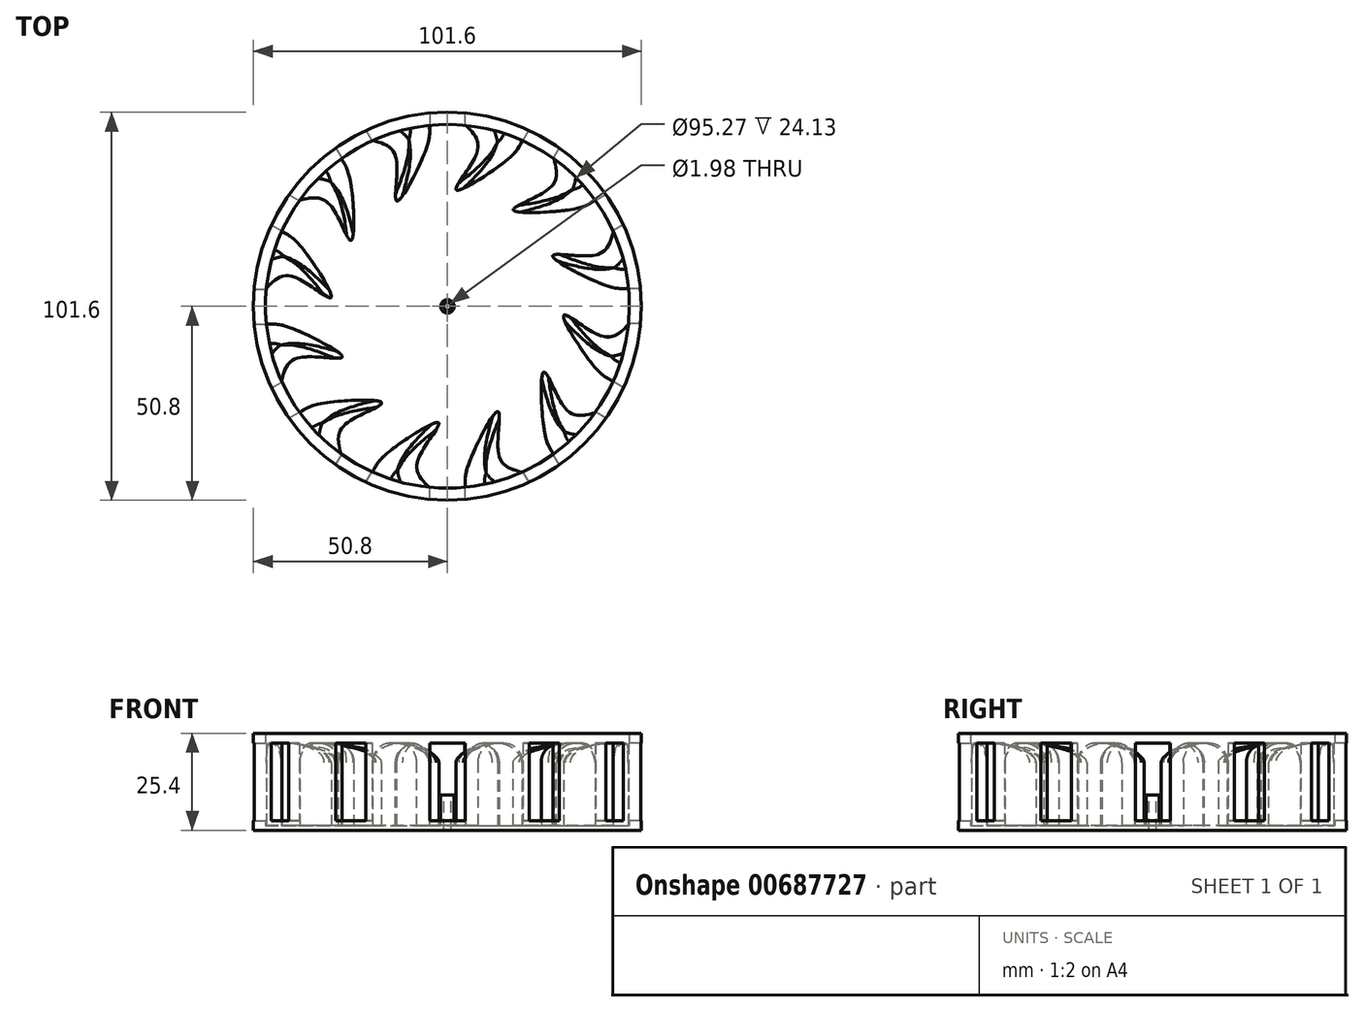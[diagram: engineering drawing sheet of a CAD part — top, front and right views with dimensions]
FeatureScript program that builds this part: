
annotation { "Feature Type Name" : "Feature", "Feature Type Description" : "" }
export const myFeature = defineFeature(function(context is Context, id is Id, definition is map)
    precondition{}
    {
        {
            var Q0;
            Q0=qCreatedBy(makeId("Top.planeOp"),FACE);
            var sketch = newSketch(context, id + "F0", { "sketchPlane" : qUnion([Q0])});
            skCircle(sketch, "E0", {"center": v(0, 0) * mm, "radius": 50.8 * mm});
            skSolve(sketch);
        }
        {
            var Q0;
            Q0=makeQuery(id+"F0.imprint","IMPRINT",FACE,{"disambiguationData":[TD([[makeQuery(id+"F0.imprint","IMPRINT",EDGE,{"derivedFrom":sQuery(id+"F0.wireOp",EDGE,"E0")}),1.0]])]});
            extrude(context, id + "F1", {"entities" : qUnion([Q0]), "depth" : 1.27 * mm, "offsetDistance" : 25.4 * mm});
        }
        {
            var Q0;
            Q0=makeQuery(id+"F1.opExtrude","CAP_FACE",FACE,{"disambiguationData":[OSD([sQuery(id+"F0.wireOp",EDGE,"E0")])],"isStart":false});
            var sketch = newSketch(context, id + "F2", { "sketchPlane" : qUnion([Q0])});
            skCircle(sketch, "E1", {"center": v(0, 0) * mm, "radius": 47.64 * mm});
            skLineSegment(sketch, "E2", {"start": v(0, 47.64) * mm, "end": v(0, -47.64) * mm});
            skLineSegment(sketch, "E3", {"start": v(-47.64, 0) * mm, "end": v(47.64, 0) * mm});
            skCircle(sketch, "E4.cCircle", {"center": v(0, 0) * mm, "radius": 17.07 * mm, "construction": true});
            skLineSegment(sketch, "E4.0", {"start": v(12.5, -12.5) * mm, "end": v(4.58, -17.07) * mm});
            skLineSegment(sketch, "E4.1", {"start": v(4.58, -17.07) * mm, "end": v(-4.57, -17.07) * mm});
            skLineSegment(sketch, "E4.2", {"start": v(-4.57, -17.07) * mm, "end": v(-12.5, -12.5) * mm});
            skLineSegment(sketch, "E4.3", {"start": v(-12.5, -12.5) * mm, "end": v(-17.07, -4.58) * mm});
            skLineSegment(sketch, "E4.4", {"start": v(-17.07, -4.58) * mm, "end": v(-17.07, 4.57) * mm});
            skLineSegment(sketch, "E4.5", {"start": v(-17.07, 4.57) * mm, "end": v(-12.5, 12.5) * mm});
            skLineSegment(sketch, "E4.6", {"start": v(-12.5, 12.5) * mm, "end": v(-4.58, 17.07) * mm});
            skLineSegment(sketch, "E4.7", {"start": v(-4.58, 17.07) * mm, "end": v(4.57, 17.07) * mm});
            skLineSegment(sketch, "E4.8", {"start": v(4.57, 17.07) * mm, "end": v(12.5, 12.5) * mm});
            skLineSegment(sketch, "E4.9", {"start": v(12.5, 12.5) * mm, "end": v(17.07, 4.58) * mm});
            skLineSegment(sketch, "E4.10", {"start": v(17.07, 4.58) * mm, "end": v(17.07, -4.57) * mm});
            skLineSegment(sketch, "E4.11", {"start": v(17.07, -4.57) * mm, "end": v(12.5, -12.5) * mm});
            skPoint(sketch, "E4.0.midPoint", {"position": v(8.54, -14.78) * mm});
            skSolve(sketch);
        }
        {
            var Q0;
            Q0=makeQuery(id+"F2.imprint","IMPRINT",FACE,{"disambiguationData":[TD([[makeQuery(id+"F2.imprint","IMPRINT",EDGE,{"derivedFrom":sQuery(id+"F2.wireOp",EDGE,"E1")}),-1.0]])]});
            extrude(context, id + "F3", {"entities" : qUnion([Q0]), "operationType" : NewBodyOperationType.ADD, "depth" : 24.13 * mm, "offsetDistance" : 25.4 * mm});
        }
        {
            var Q0;
            {var subQ0=sQuery(id+"F2.wireOp",EDGE,"E4.5");Q0=makeQuery(id+"F2.imprint","IMPRINT",FACE,{"disambiguationData":[TD([[makeQuery(id+"F2.imprint","IMPRINT",EDGE,{"derivedFrom":subQ0}),-1.0]])]});}
            var Q1;
            {var subQ0=sQuery(id+"F2.wireOp",EDGE,"E4.8");Q1=makeQuery(id+"F2.imprint","IMPRINT",FACE,{"disambiguationData":[TD([[makeQuery(id+"F2.imprint","IMPRINT",EDGE,{"derivedFrom":subQ0}),-1.0]])]});}
            var Q2;
            {var subQ1=sQuery(id+"F2.wireOp",EDGE,"E4.0");Q2=makeQuery(id+"F2.imprint","IMPRINT",FACE,{"disambiguationData":[TD([[makeQuery(id+"F2.imprint","IMPRINT",EDGE,{"derivedFrom":subQ1}),-1.0]])]});}
            var Q3;
            {var subQ0=sQuery(id+"F2.wireOp",EDGE,"E4.2");Q3=makeQuery(id+"F2.imprint","IMPRINT",FACE,{"disambiguationData":[TD([[makeQuery(id+"F2.imprint","IMPRINT",EDGE,{"derivedFrom":subQ0}),-1.0]])]});}
            extrude(context, id + "F4", {"entities" : qUnion([Q0, Q1, Q2, Q3]), "operationType" : NewBodyOperationType.ADD, "depth" : 21.59 * mm, "offsetDistance" : 25.4 * mm});
        }
        {
            var Q0;
            Q0=makeQuery(id+"F4.opExtrude","SWEPT_FACE",FACE,{"disambiguationData":[OSD([sQuery(id+"F2.wireOp",EDGE,"E4.1")])]});
            var sketch = newSketch(context, id + "F5", { "sketchPlane" : qUnion([Q0])});
            skLineSegment(sketch, "E5", {"start": v(-4.57, 2.54) * mm, "end": v(4.57, 2.54) * mm});
            skSolve(sketch);
        }
        {
            var Q0;
            Q0=makeQuery(id+"F4.opExtrude","SWEPT_FACE",FACE,{"disambiguationData":[OSD([sQuery(id+"F2.wireOp",EDGE,"E4.0")])]});
            var sketch = newSketch(context, id + "F6", { "sketchPlane" : qUnion([Q0])});
            skLineSegment(sketch, "E6", {"start": v(-4.57, 2.54) * mm, "end": v(4.57, 2.54) * mm});
            skSolve(sketch);
        }
        {
            var Q0;
            Q0=makeQuery(id+"F4.opExtrude","SWEPT_FACE",FACE,{"disambiguationData":[OSD([sQuery(id+"F2.wireOp",EDGE,"E4.11")])]});
            var sketch = newSketch(context, id + "F7", { "sketchPlane" : qUnion([Q0])});
            skLineSegment(sketch, "E7", {"start": v(-4.57, 2.54) * mm, "end": v(4.57, 2.54) * mm});
            skSolve(sketch);
        }
        {
            var Q0;
            {var subQ0=sQuery(id+"F5.wireOp",EDGE,"E5");Q0=makeQuery(id+"F5.imprint","IMPRINT",FACE,{"disambiguationData":[TD([[makeQuery(id+"F5.imprint","IMPRINT",EDGE,{"derivedFrom":subQ0}),1.0]])]});}
            extrude(context, id + "F8", {"entities" : qUnion([Q0]), "operationType" : NewBodyOperationType.REMOVE, "depth" : 50.8 * mm, "offsetDistance" : 25.4 * mm});
        }
        {
            var Q0;
            {var subQ0=sQuery(id+"F6.wireOp",EDGE,"E6");Q0=makeQuery(id+"F6.imprint","IMPRINT",FACE,{"disambiguationData":[TD([[makeQuery(id+"F6.imprint","IMPRINT",EDGE,{"derivedFrom":subQ0}),1.0]])]});}
            extrude(context, id + "F9", {"entities" : qUnion([Q0]), "operationType" : NewBodyOperationType.REMOVE, "depth" : 50.8 * mm, "offsetDistance" : 25.4 * mm});
        }
        {
            var Q0;
            {var subQ0=sQuery(id+"F7.wireOp",EDGE,"E7");Q0=makeQuery(id+"F7.imprint","IMPRINT",FACE,{"disambiguationData":[TD([[makeQuery(id+"F7.imprint","IMPRINT",EDGE,{"derivedFrom":subQ0}),1.0]])]});}
            extrude(context, id + "F10", {"entities" : qUnion([Q0]), "operationType" : NewBodyOperationType.REMOVE, "depth" : 50.8 * mm, "offsetDistance" : 25.4 * mm});
        }
        {
            var Q0;
            Q0=makeQuery(id+"F4.opExtrude","SWEPT_FACE",FACE,{"disambiguationData":[OSD([sQuery(id+"F2.wireOp",EDGE,"E4.10")])]});
            var sketch = newSketch(context, id + "F11", { "sketchPlane" : qUnion([Q0])});
            skLineSegment(sketch, "E8", {"start": v(-4.57, 2.54) * mm, "end": v(4.57, 2.54) * mm});
            skSolve(sketch);
        }
        {
            var Q0;
            Q0=makeQuery(id+"F4.opExtrude","SWEPT_FACE",FACE,{"disambiguationData":[OSD([sQuery(id+"F2.wireOp",EDGE,"E4.9")])]});
            var sketch = newSketch(context, id + "F12", { "sketchPlane" : qUnion([Q0])});
            skLineSegment(sketch, "E9", {"start": v(-4.57, 2.54) * mm, "end": v(4.57, 2.54) * mm});
            skSolve(sketch);
        }
        {
            var Q0;
            {var subQ0=sQuery(id+"F11.wireOp",EDGE,"E8");Q0=makeQuery(id+"F11.imprint","IMPRINT",FACE,{"disambiguationData":[TD([[makeQuery(id+"F11.imprint","IMPRINT",EDGE,{"derivedFrom":subQ0}),1.0]])]});}
            extrude(context, id + "F13", {"entities" : qUnion([Q0]), "operationType" : NewBodyOperationType.REMOVE, "depth" : 50.8 * mm, "offsetDistance" : 25.4 * mm});
        }
        {
            var Q0;
            {var subQ0=sQuery(id+"F12.wireOp",EDGE,"E9");Q0=makeQuery(id+"F12.imprint","IMPRINT",FACE,{"disambiguationData":[TD([[makeQuery(id+"F12.imprint","IMPRINT",EDGE,{"derivedFrom":subQ0}),1.0]])]});}
            extrude(context, id + "F14", {"entities" : qUnion([Q0]), "operationType" : NewBodyOperationType.REMOVE, "depth" : 50.8 * mm, "offsetDistance" : 25.4 * mm});
        }
        {
            var Q0;
            Q0=makeQuery(id+"F4.opExtrude","SWEPT_FACE",FACE,{"disambiguationData":[OSD([sQuery(id+"F2.wireOp",EDGE,"E4.8")])]});
            var sketch = newSketch(context, id + "F15", { "sketchPlane" : qUnion([Q0])});
            skLineSegment(sketch, "E10", {"start": v(-4.57, 2.54) * mm, "end": v(4.57, 2.54) * mm});
            skSolve(sketch);
        }
        {
            var Q0;
            Q0=makeQuery(id+"F4.opExtrude","SWEPT_FACE",FACE,{"disambiguationData":[OSD([sQuery(id+"F2.wireOp",EDGE,"E4.7")])]});
            var sketch = newSketch(context, id + "F16", { "sketchPlane" : qUnion([Q0])});
            skLineSegment(sketch, "E11", {"start": v(-4.57, 2.54) * mm, "end": v(4.57, 2.54) * mm});
            skSolve(sketch);
        }
        {
            var Q0;
            Q0=makeQuery(id+"F4.opExtrude","SWEPT_FACE",FACE,{"disambiguationData":[OSD([sQuery(id+"F2.wireOp",EDGE,"E4.6")])]});
            var sketch = newSketch(context, id + "F17", { "sketchPlane" : qUnion([Q0])});
            skLineSegment(sketch, "E12", {"start": v(-4.57, 2.54) * mm, "end": v(4.57, 2.54) * mm});
            skSolve(sketch);
        }
        {
            var Q0;
            {var subQ0=sQuery(id+"F15.wireOp",EDGE,"E10");Q0=makeQuery(id+"F15.imprint","IMPRINT",FACE,{"disambiguationData":[TD([[makeQuery(id+"F15.imprint","IMPRINT",EDGE,{"derivedFrom":subQ0}),1.0]])]});}
            extrude(context, id + "F18", {"entities" : qUnion([Q0]), "operationType" : NewBodyOperationType.REMOVE, "depth" : 50.8 * mm, "offsetDistance" : 25.4 * mm});
        }
        {
            var Q0;
            {var subQ0=sQuery(id+"F16.wireOp",EDGE,"E11");Q0=makeQuery(id+"F16.imprint","IMPRINT",FACE,{"disambiguationData":[TD([[makeQuery(id+"F16.imprint","IMPRINT",EDGE,{"derivedFrom":subQ0}),1.0]])]});}
            extrude(context, id + "F19", {"entities" : qUnion([Q0]), "operationType" : NewBodyOperationType.REMOVE, "depth" : 50.8 * mm, "offsetDistance" : 25.4 * mm});
        }
        {
            var Q0;
            {var subQ0=sQuery(id+"F17.wireOp",EDGE,"E12");Q0=makeQuery(id+"F17.imprint","IMPRINT",FACE,{"disambiguationData":[TD([[makeQuery(id+"F17.imprint","IMPRINT",EDGE,{"derivedFrom":subQ0}),1.0]])]});}
            extrude(context, id + "F20", {"entities" : qUnion([Q0]), "operationType" : NewBodyOperationType.REMOVE, "depth" : 50.8 * mm, "offsetDistance" : 25.4 * mm});
        }
        {
            var Q0;
            Q0=makeQuery(id+"F4.opExtrude","SWEPT_FACE",FACE,{"disambiguationData":[OSD([sQuery(id+"F2.wireOp",EDGE,"E4.5")])]});
            var sketch = newSketch(context, id + "F21", { "sketchPlane" : qUnion([Q0])});
            skLineSegment(sketch, "E13", {"start": v(-4.57, 2.54) * mm, "end": v(4.57, 2.54) * mm});
            skSolve(sketch);
        }
        {
            var Q0;
            Q0=makeQuery(id+"F4.opExtrude","SWEPT_FACE",FACE,{"disambiguationData":[OSD([sQuery(id+"F2.wireOp",EDGE,"E4.4")])]});
            var sketch = newSketch(context, id + "F22", { "sketchPlane" : qUnion([Q0])});
            skLineSegment(sketch, "E14", {"start": v(-4.57, 2.54) * mm, "end": v(4.57, 2.54) * mm});
            skSolve(sketch);
        }
        {
            var Q0;
            Q0=makeQuery(id+"F4.opExtrude","SWEPT_FACE",FACE,{"disambiguationData":[OSD([sQuery(id+"F2.wireOp",EDGE,"E4.3")])]});
            var sketch = newSketch(context, id + "F23", { "sketchPlane" : qUnion([Q0])});
            skLineSegment(sketch, "E15", {"start": v(-4.57, 2.54) * mm, "end": v(4.57, 2.54) * mm});
            skSolve(sketch);
        }
        {
            var Q0;
            Q0=makeQuery(id+"F4.opExtrude","SWEPT_FACE",FACE,{"disambiguationData":[OSD([sQuery(id+"F2.wireOp",EDGE,"E4.2")])]});
            var sketch = newSketch(context, id + "F24", { "sketchPlane" : qUnion([Q0])});
            skLineSegment(sketch, "E16", {"start": v(-4.57, 2.54) * mm, "end": v(4.57, 2.54) * mm});
            skSolve(sketch);
        }
        {
            var Q0;
            {var subQ0=sQuery(id+"F21.wireOp",EDGE,"E13");Q0=makeQuery(id+"F21.imprint","IMPRINT",FACE,{"disambiguationData":[TD([[makeQuery(id+"F21.imprint","IMPRINT",EDGE,{"derivedFrom":subQ0}),1.0]])]});}
            extrude(context, id + "F25", {"entities" : qUnion([Q0]), "operationType" : NewBodyOperationType.REMOVE, "depth" : 50.8 * mm, "offsetDistance" : 25.4 * mm});
        }
        {
            var Q0;
            {var subQ0=sQuery(id+"F22.wireOp",EDGE,"E14");Q0=makeQuery(id+"F22.imprint","IMPRINT",FACE,{"disambiguationData":[TD([[makeQuery(id+"F22.imprint","IMPRINT",EDGE,{"derivedFrom":subQ0}),1.0]])]});}
            extrude(context, id + "F26", {"entities" : qUnion([Q0]), "operationType" : NewBodyOperationType.REMOVE, "depth" : 50.8 * mm, "offsetDistance" : 25.4 * mm});
        }
        {
            var Q0;
            {var subQ0=sQuery(id+"F23.wireOp",EDGE,"E15");Q0=makeQuery(id+"F23.imprint","IMPRINT",FACE,{"disambiguationData":[TD([[makeQuery(id+"F23.imprint","IMPRINT",EDGE,{"derivedFrom":subQ0}),1.0]])]});}
            extrude(context, id + "F27", {"entities" : qUnion([Q0]), "operationType" : NewBodyOperationType.REMOVE, "depth" : 50.8 * mm, "offsetDistance" : 25.4 * mm});
        }
        {
            var Q0;
            {var subQ0=sQuery(id+"F24.wireOp",EDGE,"E16");Q0=makeQuery(id+"F24.imprint","IMPRINT",FACE,{"disambiguationData":[TD([[makeQuery(id+"F24.imprint","IMPRINT",EDGE,{"derivedFrom":subQ0}),1.0]])]});}
            extrude(context, id + "F28", {"entities" : qUnion([Q0]), "operationType" : NewBodyOperationType.REMOVE, "depth" : 50.8 * mm, "offsetDistance" : 25.4 * mm});
        }
        {
            var Q0;
            Q0=makeQuery(id+"F4.opExtrude","CAP_FACE",FACE,{"disambiguationData":[OSD([sQuery(id+"F2.wireOp",EDGE,"E4.0"),sQuery(id+"F2.wireOp",EDGE,"E4.1"),sQuery(id+"F2.wireOp",EDGE,"E4.2"),sQuery(id+"F2.wireOp",EDGE,"E4.3"),sQuery(id+"F2.wireOp",EDGE,"E4.4"),sQuery(id+"F2.wireOp",EDGE,"E4.5"),sQuery(id+"F2.wireOp",EDGE,"E4.6"),sQuery(id+"F2.wireOp",EDGE,"E4.7"),sQuery(id+"F2.wireOp",EDGE,"E4.8"),sQuery(id+"F2.wireOp",EDGE,"E4.9"),sQuery(id+"F2.wireOp",EDGE,"E4.10"),sQuery(id+"F2.wireOp",EDGE,"E4.11")])],"isStart":false});
            extrude(context, id + "F29", {"entities" : qUnion([Q0]), "operationType" : NewBodyOperationType.REMOVE, "oppositeDirection" : true, "depth" : 21.59 * mm, "offsetDistance" : 25.4 * mm});
        }
        {
            var Q0;
            Q0=makeQuery(id+"F29.boolean.opBoolean","MERGE",FACE,{"derivedFrom":[makeQuery(id+"F1.opExtrude","CAP_FACE",FACE,{"disambiguationData":[OSD([sQuery(id+"F0.wireOp",EDGE,"E0")])],"isStart":false}),makeQuery(id+"F29.opExtrude","CAP_FACE",FACE,{"disambiguationData":[OSD([sQuery(id+"F2.wireOp",EDGE,"E4.0"),sQuery(id+"F2.wireOp",EDGE,"E4.1"),sQuery(id+"F2.wireOp",EDGE,"E4.2"),sQuery(id+"F2.wireOp",EDGE,"E4.3"),sQuery(id+"F2.wireOp",EDGE,"E4.4"),sQuery(id+"F2.wireOp",EDGE,"E4.5"),sQuery(id+"F2.wireOp",EDGE,"E4.6"),sQuery(id+"F2.wireOp",EDGE,"E4.7"),sQuery(id+"F2.wireOp",EDGE,"E4.8"),sQuery(id+"F2.wireOp",EDGE,"E4.9"),sQuery(id+"F2.wireOp",EDGE,"E4.10"),sQuery(id+"F2.wireOp",EDGE,"E4.11")])],"isStart":false})]});
            var sketch = newSketch(context, id + "F30", { "sketchPlane" : qUnion([Q0])});
            skCircle(sketch, "E17", {"center": v(0, 0) * mm, "radius": 1 * mm});
            skCircle(sketch, "E18", {"center": v(0, 0) * mm, "radius": 1.77 * mm});
            skSolve(sketch);
        }
        {
            var Q0;
            Q0=makeQuery(id+"F30.imprint","IMPRINT",FACE,{"disambiguationData":[TD([[makeQuery(id+"F30.imprint","IMPRINT",EDGE,{"derivedFrom":sQuery(id+"F30.wireOp",EDGE,"E17")}),1.0]])]});
            extrude(context, id + "F31", {"entities" : qUnion([Q0]), "operationType" : NewBodyOperationType.REMOVE, "oppositeDirection" : true, "depth" : 25.4 * mm, "offsetDistance" : 25.4 * mm});
        }
        {
            var Q0;
            Q0=makeQuery(id+"F29.boolean.opBoolean","MERGE",FACE,{"derivedFrom":[makeQuery(id+"F1.opExtrude","CAP_FACE",FACE,{"disambiguationData":[OSD([sQuery(id+"F0.wireOp",EDGE,"E0")])],"isStart":false}),makeQuery(id+"F29.opExtrude","CAP_FACE",FACE,{"disambiguationData":[OSD([sQuery(id+"F2.wireOp",EDGE,"E4.0"),sQuery(id+"F2.wireOp",EDGE,"E4.1"),sQuery(id+"F2.wireOp",EDGE,"E4.2"),sQuery(id+"F2.wireOp",EDGE,"E4.3"),sQuery(id+"F2.wireOp",EDGE,"E4.4"),sQuery(id+"F2.wireOp",EDGE,"E4.5"),sQuery(id+"F2.wireOp",EDGE,"E4.6"),sQuery(id+"F2.wireOp",EDGE,"E4.7"),sQuery(id+"F2.wireOp",EDGE,"E4.8"),sQuery(id+"F2.wireOp",EDGE,"E4.9"),sQuery(id+"F2.wireOp",EDGE,"E4.10"),sQuery(id+"F2.wireOp",EDGE,"E4.11")])],"isStart":false})]});
            var sketch = newSketch(context, id + "F32", { "sketchPlane" : qUnion([Q0])});
            skPoint(sketch, "E19", {"position": v(-27.79, 38.7) * mm});
            skPoint(sketch, "E20", {"position": v(-38.65, 27.84) * mm});
            skPoint(sketch, "E21", {"position": v(-25.27, 17.25) * mm});
            skFitSpline(sketch, "E22", {"points": [v(-27.79, 38.7) * mm, v(-25.3, 32.18) * mm, v(-25.27, 17.25) * mm, v(-30.98, 26.8) * mm, v(-38.65, 27.84) * mm], "startDerivative": vector(13.3, -21.28) * mm, "endDerivative": vector(-36.92, -8.51) * mm});
            skPoint(sketch, "E23.1.0", {"position": v(-47.4, 4.79) * mm});
            skPoint(sketch, "E23.1.1", {"position": v(-45.36, 6.68) * mm});
            skPoint(sketch, "E23.1.2", {"position": v(-40.23, 7.73) * mm});
            skPoint(sketch, "E23.1.3", {"position": v(-30.5, 2.3) * mm});
            skPoint(sketch, "E23.1.4", {"position": v(-38, 15.22) * mm});
            skPoint(sketch, "E23.1.5", {"position": v(-41.87, 18.8) * mm});
            skPoint(sketch, "E23.1.6", {"position": v(-43.4, 19.62) * mm});
            skPoint(sketch, "E23.2.0", {"position": v(-43.44, -19.55) * mm});
            skPoint(sketch, "E23.2.1", {"position": v(-42.62, -16.89) * mm});
            skPoint(sketch, "E23.2.2", {"position": v(-38.7, -13.42) * mm});
            skPoint(sketch, "E23.2.3", {"position": v(-27.57, -13.26) * mm});
            skPoint(sketch, "E23.2.4", {"position": v(-40.52, -5.83) * mm});
            skPoint(sketch, "E23.2.5", {"position": v(-45.65, -4.66) * mm});
            skPoint(sketch, "E23.2.6", {"position": v(-47.4, -4.72) * mm});
            skPoint(sketch, "E23.3.0", {"position": v(-27.84, -38.65) * mm});
            skPoint(sketch, "E23.3.1", {"position": v(-28.47, -35.94) * mm});
            skPoint(sketch, "E23.3.2", {"position": v(-26.8, -30.98) * mm});
            skPoint(sketch, "E23.3.3", {"position": v(-17.25, -25.27) * mm});
            skPoint(sketch, "E23.3.4", {"position": v(-32.18, -25.3) * mm});
            skPoint(sketch, "E23.3.5", {"position": v(-37.2, -26.86) * mm});
            skPoint(sketch, "E23.3.6", {"position": v(-38.7, -27.79) * mm});
            skPoint(sketch, "E23.4.0", {"position": v(-4.79, -47.4) * mm});
            skPoint(sketch, "E23.4.1", {"position": v(-6.68, -45.36) * mm});
            skPoint(sketch, "E23.4.2", {"position": v(-7.73, -40.23) * mm});
            skPoint(sketch, "E23.4.3", {"position": v(-2.3, -30.5) * mm});
            skPoint(sketch, "E23.4.4", {"position": v(-15.22, -38) * mm});
            skPoint(sketch, "E23.4.5", {"position": v(-18.8, -41.87) * mm});
            skPoint(sketch, "E23.4.6", {"position": v(-19.62, -43.4) * mm});
            skPoint(sketch, "E23.5.0", {"position": v(19.55, -43.44) * mm});
            skPoint(sketch, "E23.5.1", {"position": v(16.89, -42.62) * mm});
            skPoint(sketch, "E23.5.2", {"position": v(13.42, -38.7) * mm});
            skPoint(sketch, "E23.5.3", {"position": v(13.26, -27.57) * mm});
            skPoint(sketch, "E23.5.4", {"position": v(5.83, -40.52) * mm});
            skPoint(sketch, "E23.5.5", {"position": v(4.66, -45.65) * mm});
            skPoint(sketch, "E23.5.6", {"position": v(4.72, -47.4) * mm});
            skPoint(sketch, "E23.6.0", {"position": v(38.65, -27.84) * mm});
            skPoint(sketch, "E23.6.1", {"position": v(35.94, -28.47) * mm});
            skPoint(sketch, "E23.6.2", {"position": v(30.98, -26.8) * mm});
            skPoint(sketch, "E23.6.3", {"position": v(25.27, -17.25) * mm});
            skPoint(sketch, "E23.6.4", {"position": v(25.3, -32.18) * mm});
            skPoint(sketch, "E23.6.5", {"position": v(26.86, -37.2) * mm});
            skPoint(sketch, "E23.6.6", {"position": v(27.79, -38.7) * mm});
            skPoint(sketch, "E23.7.0", {"position": v(47.4, -4.79) * mm});
            skPoint(sketch, "E23.7.1", {"position": v(45.36, -6.68) * mm});
            skPoint(sketch, "E23.7.2", {"position": v(40.23, -7.73) * mm});
            skPoint(sketch, "E23.7.3", {"position": v(30.5, -2.3) * mm});
            skPoint(sketch, "E23.7.4", {"position": v(38, -15.22) * mm});
            skPoint(sketch, "E23.7.5", {"position": v(41.87, -18.8) * mm});
            skPoint(sketch, "E23.7.6", {"position": v(43.4, -19.62) * mm});
            skPoint(sketch, "E23.8.0", {"position": v(43.44, 19.55) * mm});
            skPoint(sketch, "E23.8.1", {"position": v(42.62, 16.89) * mm});
            skPoint(sketch, "E23.8.2", {"position": v(38.7, 13.42) * mm});
            skPoint(sketch, "E23.8.3", {"position": v(27.57, 13.26) * mm});
            skPoint(sketch, "E23.8.4", {"position": v(40.52, 5.83) * mm});
            skPoint(sketch, "E23.8.5", {"position": v(45.65, 4.66) * mm});
            skPoint(sketch, "E23.8.6", {"position": v(47.4, 4.72) * mm});
            skPoint(sketch, "E23.9.0", {"position": v(27.84, 38.65) * mm});
            skPoint(sketch, "E23.9.1", {"position": v(28.47, 35.94) * mm});
            skPoint(sketch, "E23.9.2", {"position": v(26.8, 30.98) * mm});
            skPoint(sketch, "E23.9.3", {"position": v(17.25, 25.27) * mm});
            skPoint(sketch, "E23.9.4", {"position": v(32.18, 25.3) * mm});
            skPoint(sketch, "E23.9.5", {"position": v(37.2, 26.86) * mm});
            skPoint(sketch, "E23.9.6", {"position": v(38.7, 27.79) * mm});
            skPoint(sketch, "E23.10.0", {"position": v(4.79, 47.4) * mm});
            skPoint(sketch, "E23.10.1", {"position": v(6.68, 45.36) * mm});
            skPoint(sketch, "E23.10.2", {"position": v(7.73, 40.23) * mm});
            skPoint(sketch, "E23.10.3", {"position": v(2.3, 30.5) * mm});
            skPoint(sketch, "E23.10.4", {"position": v(15.22, 38) * mm});
            skPoint(sketch, "E23.10.5", {"position": v(18.8, 41.87) * mm});
            skPoint(sketch, "E23.10.6", {"position": v(19.62, 43.4) * mm});
            skPoint(sketch, "E23.11.0", {"position": v(-19.55, 43.44) * mm});
            skPoint(sketch, "E23.11.1", {"position": v(-16.89, 42.62) * mm});
            skPoint(sketch, "E23.11.2", {"position": v(-13.42, 38.7) * mm});
            skPoint(sketch, "E23.11.3", {"position": v(-13.26, 27.57) * mm});
            skPoint(sketch, "E23.11.4", {"position": v(-5.83, 40.52) * mm});
            skPoint(sketch, "E23.11.5", {"position": v(-4.66, 45.65) * mm});
            skPoint(sketch, "E23.11.6", {"position": v(-4.72, 47.4) * mm});
            skPoint(sketch, "E23.center", {"position": v(0, 0) * mm});
            skFitSpline(sketch, "E24", {"points": [v(-19.55, 43.44) * mm, v(-16.89, 42.62) * mm, v(-13.42, 38.7) * mm, v(-13.26, 27.57) * mm, v(-5.83, 40.52) * mm, v(-4.66, 45.65) * mm, v(-4.72, 47.4) * mm], "startDerivative": vector(22.34, -5.62) * mm, "endDerivative": vector(-1.05, 18.76) * mm});
            skFitSpline(sketch, "E25", {"points": [v(4.79, 47.4) * mm, v(6.68, 45.36) * mm, v(7.73, 40.23) * mm, v(2.3, 30.5) * mm, v(15.22, 38) * mm, v(18.8, 41.87) * mm, v(19.62, 43.4) * mm], "startDerivative": vector(16.54, -16.04) * mm, "endDerivative": vector(8.47, 16.77) * mm});
            skFitSpline(sketch, "E26", {"points": [v(27.84, 38.65) * mm, v(28.47, 35.94) * mm, v(26.8, 30.98) * mm, v(17.25, 25.27) * mm, v(32.18, 25.3) * mm, v(37.2, 26.86) * mm, v(38.7, 27.79) * mm], "startDerivative": vector(6.3, -22.16) * mm, "endDerivative": vector(15.72, 10.3) * mm});
            skFitSpline(sketch, "E27", {"points": [v(43.44, 19.55) * mm, v(42.62, 16.89) * mm, v(38.7, 13.42) * mm, v(27.57, 13.26) * mm, v(40.52, 5.83) * mm, v(45.65, 4.66) * mm, v(47.4, 4.72) * mm], "startDerivative": vector(-5.62, -22.34) * mm, "endDerivative": vector(18.76, 1.05) * mm});
            skFitSpline(sketch, "E28", {"points": [v(-43.4, 19.62) * mm, v(-41.87, 18.8) * mm, v(-38, 15.22) * mm, v(-30.5, 2.3) * mm, v(-40.23, 7.73) * mm, v(-45.36, 6.68) * mm, v(-47.4, 4.79) * mm], "startDerivative": vector(16.77, -8.47) * mm, "endDerivative": vector(-16.04, -16.54) * mm});
            skFitSpline(sketch, "E29", {"points": [v(-47.4, -4.72) * mm, v(-45.65, -4.66) * mm, v(-40.52, -5.83) * mm, v(-27.57, -13.26) * mm, v(-38.7, -13.42) * mm, v(-42.62, -16.89) * mm, v(-43.44, -19.55) * mm], "startDerivative": vector(18.76, 1.05) * mm, "endDerivative": vector(-5.62, -22.34) * mm});
            skFitSpline(sketch, "E30", {"points": [v(-38.7, -27.79) * mm, v(-37.2, -26.86) * mm, v(-32.18, -25.3) * mm, v(-17.25, -25.27) * mm, v(-26.8, -30.98) * mm, v(-28.47, -35.94) * mm, v(-27.84, -38.65) * mm], "startDerivative": vector(15.72, 10.3) * mm, "endDerivative": vector(6.3, -22.16) * mm});
            skFitSpline(sketch, "E31", {"points": [v(-4.79, -47.4) * mm, v(-6.68, -45.36) * mm, v(-7.73, -40.23) * mm, v(-2.3, -30.5) * mm, v(-15.22, -38) * mm, v(-18.8, -41.87) * mm, v(-19.62, -43.4) * mm], "startDerivative": vector(-16.54, 16.04) * mm, "endDerivative": vector(-8.47, -16.77) * mm});
            skFitSpline(sketch, "E32", {"points": [v(4.72, -47.4) * mm, v(4.66, -45.65) * mm, v(5.83, -40.52) * mm, v(13.26, -27.57) * mm, v(13.42, -38.7) * mm, v(16.89, -42.62) * mm, v(19.55, -43.44) * mm], "startDerivative": vector(-1.05, 18.76) * mm, "endDerivative": vector(22.34, -5.62) * mm});
            skFitSpline(sketch, "E33", {"points": [v(27.79, -38.7) * mm, v(26.86, -37.2) * mm, v(25.3, -32.18) * mm, v(25.27, -17.25) * mm, v(30.98, -26.8) * mm, v(35.94, -28.47) * mm, v(38.65, -27.84) * mm], "startDerivative": vector(-10.3, 15.72) * mm, "endDerivative": vector(22.16, 6.3) * mm});
            skFitSpline(sketch, "E34", {"points": [v(43.4, -19.62) * mm, v(41.87, -18.8) * mm, v(38, -15.22) * mm, v(30.5, -2.3) * mm, v(40.23, -7.73) * mm, v(45.36, -6.68) * mm, v(47.4, -4.79) * mm], "startDerivative": vector(-16.77, 8.47) * mm, "endDerivative": vector(16.04, 16.54) * mm});
            skSolve(sketch);
        }
        {
            var Q0;
            {var subQ0=sQuery(id+"F32.wireOp",EDGE,"E24");Q0=makeQuery(id+"F32.imprint","IMPRINT",FACE,{"disambiguationData":[TD([[makeQuery(id+"F32.imprint","IMPRINT",EDGE,{"derivedFrom":subQ0}),1.0]])]});}
            var Q1;
            {var subQ0=sQuery(id+"F32.wireOp",EDGE,"E25");Q1=makeQuery(id+"F32.imprint","IMPRINT",FACE,{"disambiguationData":[TD([[makeQuery(id+"F32.imprint","IMPRINT",EDGE,{"derivedFrom":subQ0}),1.0]])]});}
            var Q2;
            {var subQ0=sQuery(id+"F32.wireOp",EDGE,"E26");Q2=makeQuery(id+"F32.imprint","IMPRINT",FACE,{"disambiguationData":[TD([[makeQuery(id+"F32.imprint","IMPRINT",EDGE,{"derivedFrom":subQ0}),1.0]])]});}
            var Q3;
            {var subQ0=sQuery(id+"F32.wireOp",EDGE,"E27");Q3=makeQuery(id+"F32.imprint","IMPRINT",FACE,{"disambiguationData":[TD([[makeQuery(id+"F32.imprint","IMPRINT",EDGE,{"derivedFrom":subQ0}),1.0]])]});}
            var Q4;
            {var subQ0=sQuery(id+"F32.wireOp",EDGE,"E34");Q4=makeQuery(id+"F32.imprint","IMPRINT",FACE,{"disambiguationData":[TD([[makeQuery(id+"F32.imprint","IMPRINT",EDGE,{"derivedFrom":subQ0}),-1.0]])]});}
            var Q5;
            {var subQ0=sQuery(id+"F32.wireOp",EDGE,"E33");Q5=makeQuery(id+"F32.imprint","IMPRINT",FACE,{"disambiguationData":[TD([[makeQuery(id+"F32.imprint","IMPRINT",EDGE,{"derivedFrom":subQ0}),-1.0]])]});}
            var Q6;
            {var subQ0=sQuery(id+"F32.wireOp",EDGE,"E32");Q6=makeQuery(id+"F32.imprint","IMPRINT",FACE,{"disambiguationData":[TD([[makeQuery(id+"F32.imprint","IMPRINT",EDGE,{"derivedFrom":subQ0}),-1.0]])]});}
            var Q7;
            {var subQ0=sQuery(id+"F32.wireOp",EDGE,"E31");Q7=makeQuery(id+"F32.imprint","IMPRINT",FACE,{"disambiguationData":[TD([[makeQuery(id+"F32.imprint","IMPRINT",EDGE,{"derivedFrom":subQ0}),1.0]])]});}
            var Q8;
            {var subQ0=sQuery(id+"F32.wireOp",EDGE,"E30");Q8=makeQuery(id+"F32.imprint","IMPRINT",FACE,{"disambiguationData":[TD([[makeQuery(id+"F32.imprint","IMPRINT",EDGE,{"derivedFrom":subQ0}),-1.0]])]});}
            var Q9;
            {var subQ0=sQuery(id+"F32.wireOp",EDGE,"E29");Q9=makeQuery(id+"F32.imprint","IMPRINT",FACE,{"disambiguationData":[TD([[makeQuery(id+"F32.imprint","IMPRINT",EDGE,{"derivedFrom":subQ0}),-1.0]])]});}
            var Q10;
            {var subQ0=sQuery(id+"F32.wireOp",EDGE,"E28");Q10=makeQuery(id+"F32.imprint","IMPRINT",FACE,{"disambiguationData":[TD([[makeQuery(id+"F32.imprint","IMPRINT",EDGE,{"derivedFrom":subQ0}),-1.0]])]});}
            var Q11;
            {var subQ0=sQuery(id+"F32.wireOp",EDGE,"E22");Q11=makeQuery(id+"F32.imprint","IMPRINT",FACE,{"disambiguationData":[TD([[makeQuery(id+"F32.imprint","IMPRINT",EDGE,{"derivedFrom":subQ0}),-1.0]])]});}
            extrude(context, id + "F33", {"entities" : qUnion([Q0, Q1, Q2, Q3, Q4, Q5, Q6, Q7, Q8, Q9, Q10, Q11]), "operationType" : NewBodyOperationType.ADD, "depth" : 21.59 * mm, "offsetDistance" : 25.4 * mm});
        }
        {
            var Q0;
            Q0=makeQuery(id+"F33.opExtrude","CAP_EDGE",EDGE,{"disambiguationData":[OSD([sQuery(id+"F32.wireOp",EDGE,"E31")])],"isStart":false});
            var Q1;
            Q1=makeQuery(id+"F33.opExtrude","CAP_EDGE",EDGE,{"disambiguationData":[OSD([sQuery(id+"F32.wireOp",EDGE,"E30")])],"isStart":false});
            var Q2;
            Q2=makeQuery(id+"F33.opExtrude","CAP_EDGE",EDGE,{"disambiguationData":[OSD([sQuery(id+"F32.wireOp",EDGE,"E29")])],"isStart":false});
            var Q3;
            Q3=makeQuery(id+"F33.opExtrude","CAP_EDGE",EDGE,{"disambiguationData":[OSD([sQuery(id+"F32.wireOp",EDGE,"E32")])],"isStart":false});
            var Q4;
            Q4=makeQuery(id+"F33.opExtrude","CAP_EDGE",EDGE,{"disambiguationData":[OSD([sQuery(id+"F32.wireOp",EDGE,"E33")])],"isStart":false});
            var Q5;
            Q5=makeQuery(id+"F33.opExtrude","CAP_EDGE",EDGE,{"disambiguationData":[OSD([sQuery(id+"F32.wireOp",EDGE,"E34")])],"isStart":false});
            var Q6;
            Q6=makeQuery(id+"F33.opExtrude","CAP_EDGE",EDGE,{"disambiguationData":[OSD([sQuery(id+"F32.wireOp",EDGE,"E27")])],"isStart":false});
            var Q7;
            Q7=makeQuery(id+"F33.opExtrude","CAP_EDGE",EDGE,{"disambiguationData":[OSD([sQuery(id+"F32.wireOp",EDGE,"E26")])],"isStart":false});
            var Q8;
            Q8=makeQuery(id+"F33.opExtrude","CAP_EDGE",EDGE,{"disambiguationData":[OSD([sQuery(id+"F32.wireOp",EDGE,"E24")])],"isStart":false});
            var Q9;
            Q9=makeQuery(id+"F33.opExtrude","CAP_EDGE",EDGE,{"disambiguationData":[OSD([sQuery(id+"F32.wireOp",EDGE,"E25")])],"isStart":false});
            var Q10;
            Q10=makeQuery(id+"F33.opExtrude","CAP_EDGE",EDGE,{"disambiguationData":[OSD([sQuery(id+"F32.wireOp",EDGE,"E22")])],"isStart":false});
            var Q11;
            Q11=makeQuery(id+"F33.opExtrude","CAP_EDGE",EDGE,{"disambiguationData":[OSD([sQuery(id+"F32.wireOp",EDGE,"E28")])],"isStart":false});
            fillet(context, id + "F34", {"entities" : qUnion([Q0, Q1, Q2, Q3, Q4, Q5, Q6, Q7, Q8, Q9, Q10, Q11]), "radius" : 5.08 * mm, "tangentPropagation" : true, "allowEdgeOverflow" : false});
        }
        {
            var Q0;
            Q0=makeQuery(id+"F30.imprint","IMPRINT",FACE,{"disambiguationData":[TD([[makeQuery(id+"F30.imprint","IMPRINT",EDGE,{"derivedFrom":sQuery(id+"F30.wireOp",EDGE,"E17")}),-1.0]])]});
            extrude(context, id + "F35", {"entities" : qUnion([Q0]), "operationType" : NewBodyOperationType.ADD, "depth" : 7.98 * mm, "offsetDistance" : 25.4 * mm});
        }
    });
